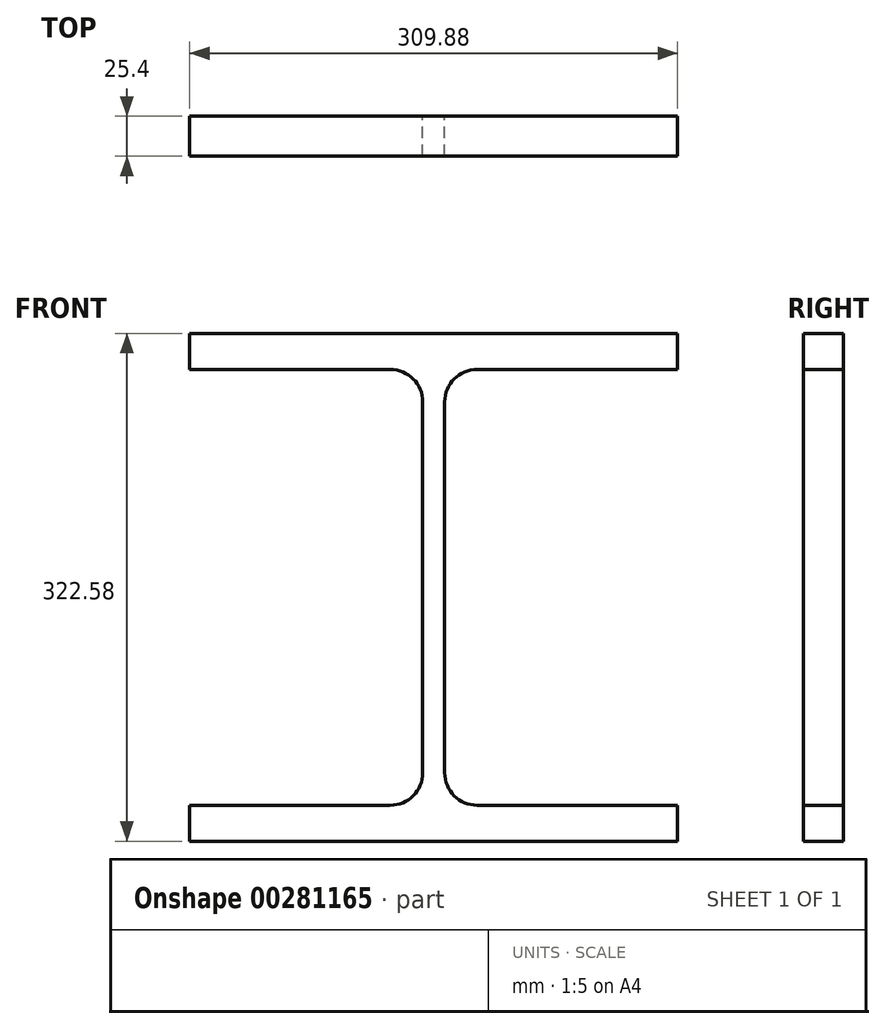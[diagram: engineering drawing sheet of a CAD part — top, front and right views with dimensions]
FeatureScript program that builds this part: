
annotation { "Feature Type Name" : "Feature", "Feature Type Description" : "" }
export const myFeature = defineFeature(function(context is Context, id is Id, definition is map)
    precondition{}
    {
        {
            var Q0;
            Q0=qCreatedBy(makeId("Front.planeOp"),FACE);
            var sketch = newSketch(context, id + "F0", { "sketchPlane" : qUnion([Q0])});
            skLineSegment(sketch, "E0.bottom", {"start": v(-154.94, 161.3) * mm, "end": v(154.94, 161.3) * mm});
            skLineSegment(sketch, "E0.top", {"start": v(-154.94, -161.3) * mm, "end": v(154.94, -161.3) * mm});
            skLineSegment(sketch, "E0.left", {"start": v(-154.94, 161.29) * mm, "end": v(-154.94, -161.3) * mm, "construction": true});
            skLineSegment(sketch, "E0.right", {"start": v(154.94, 161.29) * mm, "end": v(154.94, -161.3) * mm, "construction": true});
            skPoint(sketch, "E0.middle", {"position": v(0, 0) * mm});
            skLineSegment(sketch, "E1", {"start": v(-154.94, 161.29) * mm, "end": v(-154.94, 138.43) * mm});
            skLineSegment(sketch, "E2", {"start": v(-154.94, 138.43) * mm, "end": v(-27.62, 138.43) * mm});
            skLineSegment(sketch, "E3", {"start": v(-6.98, 117.8) * mm, "end": v(-6.98, -117.8) * mm});
            skLineSegment(sketch, "E4", {"start": v(-27.62, -138.43) * mm, "end": v(-154.94, -138.43) * mm});
            skLineSegment(sketch, "E5", {"start": v(-154.94, -138.43) * mm, "end": v(-154.94, -161.3) * mm});
            skLineSegment(sketch, "E6", {"start": v(154.94, 161.29) * mm, "end": v(154.94, 138.43) * mm});
            skLineSegment(sketch, "E7", {"start": v(154.94, 138.43) * mm, "end": v(27.62, 138.43) * mm});
            skLineSegment(sketch, "E8", {"start": v(6.99, 117.8) * mm, "end": v(6.99, -117.8) * mm});
            skLineSegment(sketch, "E9", {"start": v(27.62, -138.43) * mm, "end": v(154.94, -138.43) * mm});
            skLineSegment(sketch, "E10", {"start": v(154.94, -138.43) * mm, "end": v(154.94, -161.3) * mm});
            skPoint(sketch, "E11.visualSharp", {"position": v(-6.99, 138.43) * mm});
            skArc(sketch, "E11.filletArc", {"start": v(-6.98, 117.8) * mm, "mid": v(-13.03, 132.39) * mm, "end": v(-27.62, 138.43) * mm});
            skPoint(sketch, "E12.visualSharp", {"position": v(6.98, 138.43) * mm});
            skArc(sketch, "E12.filletArc", {"start": v(27.62, 138.43) * mm, "mid": v(13.03, 132.39) * mm, "end": v(6.98, 117.8) * mm});
            skPoint(sketch, "E13.visualSharp", {"position": v(6.98, -138.43) * mm});
            skArc(sketch, "E13.filletArc", {"start": v(6.99, -117.8) * mm, "mid": v(13.03, -132.39) * mm, "end": v(27.62, -138.43) * mm});
            skPoint(sketch, "E14.visualSharp", {"position": v(-6.99, -138.43) * mm});
            skArc(sketch, "E14.filletArc", {"start": v(-27.62, -138.43) * mm, "mid": v(-13.03, -132.39) * mm, "end": v(-6.98, -117.8) * mm});
            skSolve(sketch);
        }
        {
            var Q0;
            Q0 = qSketchRegion(id + "F0", true);
            extrude(context, id + "F1", {"entities" : qUnion([Q0]), "depth" : 25.4 * mm});
        }
    });
